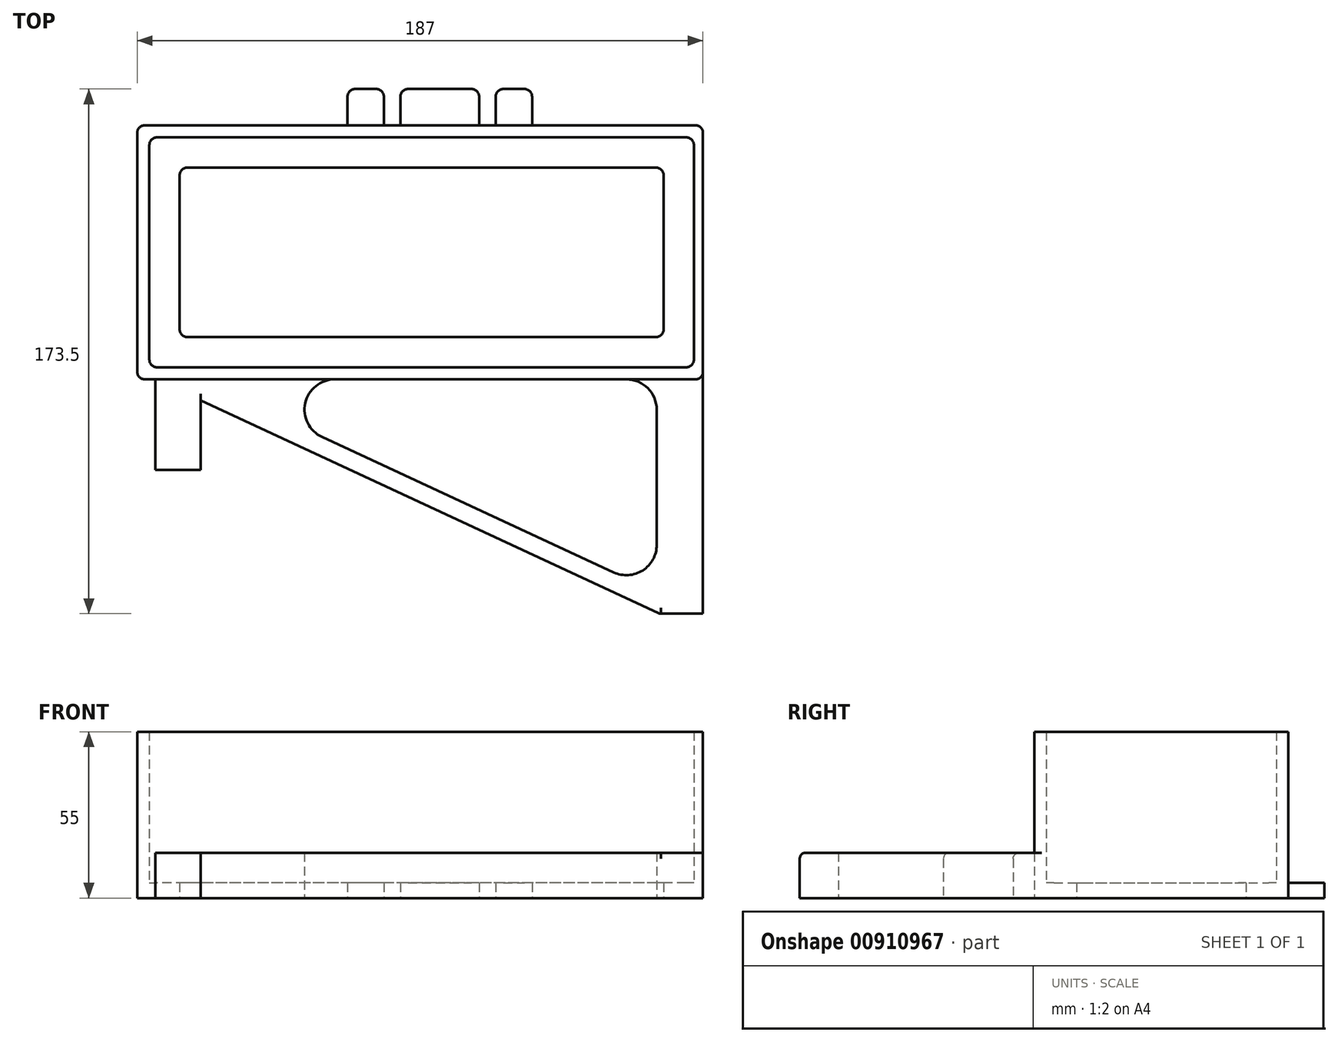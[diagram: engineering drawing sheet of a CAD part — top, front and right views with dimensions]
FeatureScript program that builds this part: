
annotation { "Feature Type Name" : "Feature", "Feature Type Description" : "" }
export const myFeature = defineFeature(function(context is Context, id is Id, definition is map)
    precondition{}
    {
        {
            var Q0;
            Q0=qCreatedBy(makeId("Top.planeOp"),FACE);
            var sketch = newSketch(context, id + "F0", { "sketchPlane" : qUnion([Q0])});
            skLineSegment(sketch, "E0.bottom", {"start": v(87.5, 0) * mm, "end": v(-87.5, 0) * mm});
            skLineSegment(sketch, "E0.top", {"start": v(87.5, 76) * mm, "end": v(-87.5, 76) * mm});
            skLineSegment(sketch, "E0.left", {"start": v(90, 2.5) * mm, "end": v(90, 73.5) * mm});
            skLineSegment(sketch, "E0.right", {"start": v(-90, 2.5) * mm, "end": v(-90, 73.5) * mm});
            skLineSegment(sketch, "E1.0", {"start": v(102, 80) * mm, "end": v(-74, 80) * mm});
            skLineSegment(sketch, "E2.0", {"start": v(-94, 0) * mm, "end": v(-94, 76) * mm});
            skLineSegment(sketch, "E3.0", {"start": v(67.7, -4) * mm, "end": v(-28.7, -4) * mm});
            skLineSegment(sketch, "E4.0", {"start": v(93, 0) * mm, "end": v(93, 76) * mm});
            skLineSegment(sketch, "E5", {"start": v(-74, 80) * mm, "end": v(-91.5, 80) * mm});
            skLineSegment(sketch, "E6", {"start": v(-94, 76) * mm, "end": v(-94, 77.5) * mm});
            skLineSegment(sketch, "E7", {"start": v(-94, -1.5) * mm, "end": v(-94, 0) * mm});
            skLineSegment(sketch, "E8", {"start": v(-88, -4) * mm, "end": v(-91.5, -4) * mm});
            skLineSegment(sketch, "E9", {"start": v(90.5, 80) * mm, "end": v(102, 80) * mm});
            skLineSegment(sketch, "E10", {"start": v(93, 77.5) * mm, "end": v(93, 76) * mm});
            skLineSegment(sketch, "E11", {"start": v(88, -4) * mm, "end": v(90.5, -4) * mm});
            skLineSegment(sketch, "E12", {"start": v(93, -1.5) * mm, "end": v(93, 0) * mm});
            skLineSegment(sketch, "E13", {"start": v(-7, 80) * mm, "end": v(-7, 89.5) * mm});
            skLineSegment(sketch, "E14", {"start": v(-4.5, 92) * mm, "end": v(16.5, 92) * mm});
            skLineSegment(sketch, "E15", {"start": v(19, 89.5) * mm, "end": v(19, 80) * mm});
            skLineSegment(sketch, "E16", {"start": v(6, 92) * mm, "end": v(6, 80) * mm, "construction": true});
            skLineSegment(sketch, "E17", {"start": v(6, 80) * mm, "end": v(6, 76) * mm, "construction": true});
            skLineSegment(sketch, "E18", {"start": v(-12.5, 80) * mm, "end": v(-12.5, 89.5) * mm});
            skLineSegment(sketch, "E19", {"start": v(-15, 92) * mm, "end": v(-22, 92) * mm});
            skLineSegment(sketch, "E20", {"start": v(-24.5, 89.5) * mm, "end": v(-24.5, 80) * mm});
            skLineSegment(sketch, "E21", {"start": v(24.5, 80) * mm, "end": v(24.5, 89.5) * mm});
            skLineSegment(sketch, "E22", {"start": v(27, 92) * mm, "end": v(34, 92) * mm});
            skLineSegment(sketch, "E23", {"start": v(36.5, 89.5) * mm, "end": v(36.5, 80) * mm});
            skPoint(sketch, "E24.visualSharp", {"position": v(19, 92) * mm});
            skArc(sketch, "E24.filletArc", {"start": v(19, 89.5) * mm, "mid": v(18.27, 91.27) * mm, "end": v(16.5, 92) * mm});
            skPoint(sketch, "E25.visualSharp", {"position": v(-7, 92) * mm});
            skArc(sketch, "E25.filletArc", {"start": v(-4.5, 92) * mm, "mid": v(-6.27, 91.27) * mm, "end": v(-7, 89.5) * mm});
            skPoint(sketch, "E26.visualSharp", {"position": v(-12.5, 92) * mm});
            skArc(sketch, "E26.filletArc", {"start": v(-12.5, 89.5) * mm, "mid": v(-13.23, 91.27) * mm, "end": v(-15, 92) * mm});
            skPoint(sketch, "E27.visualSharp", {"position": v(24.5, 92) * mm});
            skArc(sketch, "E27.filletArc", {"start": v(27, 92) * mm, "mid": v(25.23, 91.27) * mm, "end": v(24.5, 89.5) * mm});
            skPoint(sketch, "E28.visualSharp", {"position": v(-24.5, 92) * mm});
            skArc(sketch, "E28.filletArc", {"start": v(-22, 92) * mm, "mid": v(-23.77, 91.27) * mm, "end": v(-24.5, 89.5) * mm});
            skPoint(sketch, "E29.visualSharp", {"position": v(36.5, 92) * mm});
            skArc(sketch, "E29.filletArc", {"start": v(36.5, 89.5) * mm, "mid": v(35.77, 91.27) * mm, "end": v(34, 92) * mm});
            skPoint(sketch, "E30.visualSharp", {"position": v(-90, 76) * mm});
            skArc(sketch, "E30.filletArc", {"start": v(-87.5, 76) * mm, "mid": v(-89.27, 75.27) * mm, "end": v(-90, 73.5) * mm});
            skPoint(sketch, "E31.visualSharp", {"position": v(-94, 80) * mm});
            skArc(sketch, "E31.filletArc", {"start": v(-91.5, 80) * mm, "mid": v(-93.27, 79.27) * mm, "end": v(-94, 77.5) * mm});
            skPoint(sketch, "E32.visualSharp", {"position": v(-90, 0) * mm});
            skArc(sketch, "E32.filletArc", {"start": v(-90, 2.5) * mm, "mid": v(-89.27, 0.73) * mm, "end": v(-87.5, 0) * mm});
            skPoint(sketch, "E33.visualSharp", {"position": v(-94, -4) * mm});
            skArc(sketch, "E33.filletArc", {"start": v(-94, -1.5) * mm, "mid": v(-93.27, -3.27) * mm, "end": v(-91.5, -4) * mm});
            skPoint(sketch, "E34.visualSharp", {"position": v(93, -4) * mm});
            skArc(sketch, "E34.filletArc", {"start": v(90.5, -4) * mm, "mid": v(92.27, -3.27) * mm, "end": v(93, -1.5) * mm});
            skPoint(sketch, "E35.visualSharp", {"position": v(90, 0) * mm});
            skArc(sketch, "E35.filletArc", {"start": v(87.5, 0) * mm, "mid": v(89.27, 0.73) * mm, "end": v(90, 2.5) * mm});
            skPoint(sketch, "E36.visualSharp", {"position": v(90, 76) * mm});
            skArc(sketch, "E36.filletArc", {"start": v(90, 73.5) * mm, "mid": v(89.27, 75.27) * mm, "end": v(87.5, 76) * mm});
            skPoint(sketch, "E37.visualSharp", {"position": v(93, 80) * mm});
            skArc(sketch, "E37.filletArc", {"start": v(93, 77.5) * mm, "mid": v(92.27, 79.27) * mm, "end": v(90.5, 80) * mm});
            skLineSegment(sketch, "E38.0", {"start": v(77.5, 66) * mm, "end": v(-77.5, 66) * mm});
            skLineSegment(sketch, "E39.0", {"start": v(80, 12.5) * mm, "end": v(80, 63.5) * mm});
            skLineSegment(sketch, "E40.0", {"start": v(77.5, 10) * mm, "end": v(-77.5, 10) * mm});
            skLineSegment(sketch, "E41.0", {"start": v(-80, 12.5) * mm, "end": v(-80, 63.5) * mm});
            skPoint(sketch, "E42.visualSharp", {"position": v(-80, 66) * mm});
            skArc(sketch, "E42.filletArc", {"start": v(-77.5, 66) * mm, "mid": v(-79.27, 65.27) * mm, "end": v(-80, 63.5) * mm});
            skPoint(sketch, "E43.visualSharp", {"position": v(-80, 10) * mm});
            skArc(sketch, "E43.filletArc", {"start": v(-80, 12.5) * mm, "mid": v(-79.27, 10.73) * mm, "end": v(-77.5, 10) * mm});
            skPoint(sketch, "E44.visualSharp", {"position": v(80, 66) * mm});
            skArc(sketch, "E44.filletArc", {"start": v(80, 63.5) * mm, "mid": v(79.27, 65.27) * mm, "end": v(77.5, 66) * mm});
            skPoint(sketch, "E45.visualSharp", {"position": v(80, 10) * mm});
            skArc(sketch, "E45.filletArc", {"start": v(77.5, 10) * mm, "mid": v(79.27, 10.73) * mm, "end": v(80, 12.5) * mm});
            skLineSegment(sketch, "E46", {"start": v(93, -1.5) * mm, "end": v(93, -81.5) * mm});
            skLineSegment(sketch, "E47", {"start": v(93, -81.5) * mm, "end": v(78.7, -81.5) * mm});
            skLineSegment(sketch, "E48", {"start": v(-88, -4) * mm, "end": v(-88, -34) * mm});
            skLineSegment(sketch, "E49", {"start": v(-88, -34) * mm, "end": v(-73, -34) * mm});
            skLineSegment(sketch, "E50", {"start": v(-73, -34) * mm, "end": v(-73, -4) * mm});
            skLineSegment(sketch, "E51", {"start": v(-88, -4) * mm, "end": v(78.7, -81.5) * mm});
            skLineSegment(sketch, "E52", {"start": v(63.5, -67.8) * mm, "end": v(-32.9, -23.07) * mm});
            skArc(sketch, "E53.filletArc", {"start": v(77.7, -14) * mm, "mid": v(74.78, -6.93) * mm, "end": v(67.7, -4) * mm});
            skLineSegment(sketch, "E54", {"start": v(67.7, -4) * mm, "end": v(88, -4) * mm});
            skLineSegment(sketch, "E55", {"start": v(77.7, -14) * mm, "end": v(77.7, -58.74) * mm});
            skLineSegment(sketch, "E56", {"start": v(78.7, -74.4) * mm, "end": v(78.7, -81.5) * mm});
            skArc(sketch, "E57.filletArc", {"start": v(63.5, -67.8) * mm, "mid": v(73.09, -67.17) * mm, "end": v(77.7, -58.74) * mm});
            skPoint(sketch, "E58.newPointA", {"position": v(-88, -4) * mm});
            skArc(sketch, "E58.filletArc", {"start": v(-28.7, -4) * mm, "mid": v(-38.46, -11.84) * mm, "end": v(-32.9, -23.07) * mm});
            skLineSegment(sketch, "E59", {"start": v(-28.7, -4) * mm, "end": v(-88, -4) * mm});
            skSolve(sketch);
        }
        {
            var Q0;
            Q0=makeQuery(id+"F0.imprint","IMPRINT",FACE,{"disambiguationData":[TD([[makeQuery(id+"F0.imprint","IMPRINT",EDGE,{"derivedFrom":sQuery(id+"F0.wireOp",EDGE,"E0.bottom")}),1.0]])]});
            extrude(context, id + "F1", {"entities" : qUnion([Q0]), "depth" : 55 * mm, "offsetDistance" : 25 * mm});
        }
        {
            var Q0;
            Q0=makeQuery(id+"F0.imprint","IMPRINT",FACE,{"disambiguationData":[TD([[makeQuery(id+"F0.imprint","IMPRINT",EDGE,{"derivedFrom":sQuery(id+"F0.wireOp",EDGE,"E0.bottom")}),-1.0]])]});
            var Q1;
            {var subQ1=sQuery(id+"F0.wireOp",EDGE,"E18");Q1=makeQuery(id+"F0.imprint","IMPRINT",FACE,{"disambiguationData":[TD([[makeQuery(id+"F0.imprint","IMPRINT",EDGE,{"derivedFrom":subQ1}),1.0]])]});}
            var Q2;
            {var subQ1=sQuery(id+"F0.wireOp",EDGE,"E13");Q2=makeQuery(id+"F0.imprint","IMPRINT",FACE,{"disambiguationData":[TD([[makeQuery(id+"F0.imprint","IMPRINT",EDGE,{"derivedFrom":subQ1}),-1.0]])]});}
            var Q3;
            {var subQ0=sQuery(id+"F0.wireOp",EDGE,"E21");Q3=makeQuery(id+"F0.imprint","IMPRINT",FACE,{"disambiguationData":[TD([[makeQuery(id+"F0.imprint","IMPRINT",EDGE,{"derivedFrom":subQ0}),-1.0]])]});}
            extrude(context, id + "F2", {"entities" : qUnion([Q0, Q1, Q2, Q3]), "operationType" : NewBodyOperationType.ADD, "depth" : 5 * mm, "offsetDistance" : 25 * mm});
        }
        {
            var Q0;
            {var subQ0=sQuery(id+"F0.wireOp",EDGE,"E11");Q0=makeQuery(id+"F0.imprint","IMPRINT",FACE,{"disambiguationData":[TD([[makeQuery(id+"F0.imprint","IMPRINT",EDGE,{"derivedFrom":subQ0}),-1.0]])]});}
            var Q1;
            {var subQ0=sQuery(id+"F0.wireOp",EDGE,"E47");Q1=makeQuery(id+"F0.imprint","IMPRINT",FACE,{"disambiguationData":[TD([[makeQuery(id+"F0.imprint","IMPRINT",EDGE,{"derivedFrom":subQ0}),-1.0]])]});}
            extrude(context, id + "F3", {"entities" : qUnion([Q0, Q1]), "operationType" : NewBodyOperationType.ADD, "depth" : 15 * mm, "offsetDistance" : 25 * mm});
        }
        {
            var Q0;
            {var subQ1=sQuery(id+"F0.wireOp",EDGE,"Ny0Gnn2i-Ygqb-VPq2-N1I1-QU3OLZ8xniGR");var subQ3=sQuery(id+"F0.wireOp",EDGE,"E52");var subQ4=makeQuery(id+"F0.imprint","INTERSECT",VERTEX,{"derivedFrom":[subQ1,subQ3]});Q0=makeQuery(id+"F0.imprint","IMPRINT",FACE,{"disambiguationData":[TD([[makeQuery(id+"F0.imprint","IMPRINT",EDGE,{"disambiguationData":[TD([[subQ4,1.0]])],"derivedFrom":subQ1}),1.0]])]});}
            var Q1;
            {var subQ0=sQuery(id+"F0.wireOp",EDGE,"E59");var subQ5=sQuery(id+"F0.wireOp",EDGE,"E50");var subQ6=makeQuery(id+"F0.imprint","INTERSECT",VERTEX,{"derivedFrom":[subQ5,subQ0]});Q1=makeQuery(id+"F0.imprint","IMPRINT",FACE,{"disambiguationData":[TD([[makeQuery(id+"F0.imprint","IMPRINT",EDGE,{"disambiguationData":[TD([[subQ6,1.0]])],"derivedFrom":subQ5}),1.0]])]});}
            var Q2;
            {var subQ0=sQuery(id+"F0.wireOp",EDGE,"fGbPgxKb-3OdY-1Y91-8G2S-CM4cBlenFRyz");Q2=makeQuery(id+"F0.imprint","IMPRINT",FACE,{"disambiguationData":[TD([[makeQuery(id+"F0.imprint","IMPRINT",EDGE,{"derivedFrom":subQ0}),1.0]])]});}
            var Q3;
            {var subQ0=sQuery(id+"F0.wireOp",EDGE,"E48");Q3=makeQuery(id+"F0.imprint","IMPRINT",FACE,{"disambiguationData":[TD([[makeQuery(id+"F0.imprint","IMPRINT",EDGE,{"derivedFrom":subQ0}),1.0]])]});}
            extrude(context, id + "F4", {"entities" : qUnion([Q0, Q1, Q2, Q3]), "operationType" : NewBodyOperationType.ADD, "depth" : 15 * mm, "offsetDistance" : 25 * mm});
        }
        {
            var Q0;
            Q0=makeQuery(id+"F3.opExtrude","CAP_EDGE",EDGE,{"disambiguationData":[OSD([sQuery(id+"F0.wireOp",EDGE,"E47")])],"isStart":false});
            fillet(context, id + "F5", {"entities" : qUnion([Q0]), "radius" : 2 * mm, "tangentPropagation" : true, "allowEdgeOverflow" : false});
        }
        {
            var Q0;
            Q0=makeQuery(id+"F3.opExtrude","CAP_EDGE",EDGE,{"disambiguationData":[OSD([sQuery(id+"F0.wireOp",EDGE,"E51")])],"isStart":false});
            fillet(context, id + "F6", {"entities" : qUnion([Q0]), "radius" : 2 * mm, "tangentPropagation" : true, "allowEdgeOverflow" : false});
        }
        {
            var Q0;
            Q0=makeQuery(id+"F4.opExtrude","CAP_EDGE",EDGE,{"disambiguationData":[OSD([sQuery(id+"F0.wireOp",EDGE,"E49")])],"isStart":false});
            fillet(context, id + "F7", {"entities" : qUnion([Q0]), "radius" : 2 * mm, "tangentPropagation" : true, "allowEdgeOverflow" : false});
        }
    });
